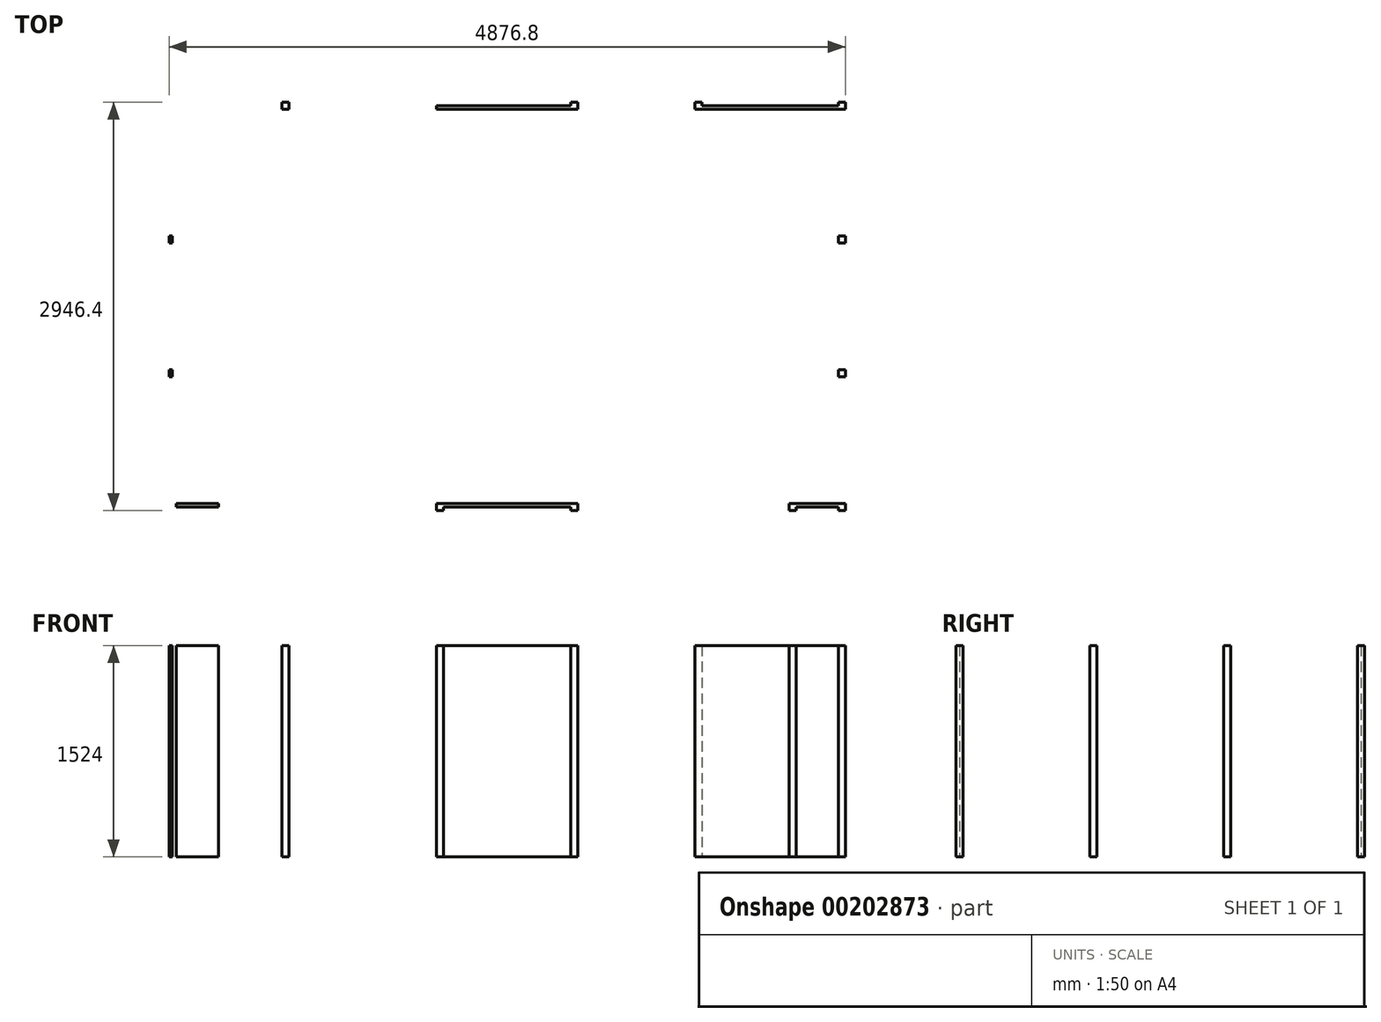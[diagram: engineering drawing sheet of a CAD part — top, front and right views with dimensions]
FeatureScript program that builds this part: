
annotation { "Feature Type Name" : "Feature", "Feature Type Description" : "" }
export const myFeature = defineFeature(function(context is Context, id is Id, definition is map)
    precondition{}
    {
        {
            var Q0;
            Q0=qCreatedBy(makeId("Top.planeOp"),FACE);
            var sketch = newSketch(context, id + "F0", { "sketchPlane" : qUnion([Q0])});
            skLineSegment(sketch, "E0.bottom", {"start": v(-61.33, -50.8) * mm, "end": v(-10.53, -50.8) * mm});
            skLineSegment(sketch, "E0.top", {"start": v(-61.33, 0) * mm, "end": v(-10.53, 0) * mm});
            skLineSegment(sketch, "E0.left", {"start": v(-61.33, -50.8) * mm, "end": v(-61.33, 0) * mm});
            skLineSegment(sketch, "E0.right", {"start": v(-10.53, -50.8) * mm, "end": v(-10.53, 0) * mm});
            skLineSegment(sketch, "E1.bottom", {"start": v(294.27, -50.8) * mm, "end": v(345.07, -50.8) * mm});
            skLineSegment(sketch, "E1.top", {"start": v(294.27, 0) * mm, "end": v(345.07, 0) * mm});
            skLineSegment(sketch, "E1.left", {"start": v(294.27, -50.8) * mm, "end": v(294.27, 0) * mm});
            skLineSegment(sketch, "E1.right", {"start": v(345.07, -50.8) * mm, "end": v(345.07, 0) * mm});
            skLineSegment(sketch, "E2.bottom", {"start": v(1869.07, -50.8) * mm, "end": v(1919.87, -50.8) * mm});
            skLineSegment(sketch, "E2.top", {"start": v(1869.07, 0) * mm, "end": v(1919.87, 0) * mm});
            skLineSegment(sketch, "E2.left", {"start": v(1869.07, -50.8) * mm, "end": v(1869.07, 0) * mm});
            skLineSegment(sketch, "E2.right", {"start": v(1919.87, -50.8) * mm, "end": v(1919.87, 0) * mm});
            skLineSegment(sketch, "E3.bottom", {"start": v(-61.33, 914.4) * mm, "end": v(-10.53, 914.4) * mm});
            skLineSegment(sketch, "E3.top", {"start": v(-61.33, 965.2) * mm, "end": v(-10.53, 965.2) * mm});
            skLineSegment(sketch, "E3.left", {"start": v(-61.33, 914.4) * mm, "end": v(-61.33, 965.2) * mm});
            skLineSegment(sketch, "E3.right", {"start": v(-10.53, 914.4) * mm, "end": v(-10.53, 965.2) * mm});
            skLineSegment(sketch, "E4.MirrorCS", {"start": v(4815.47, 965.2) * mm, "end": v(4764.67, 965.2) * mm});
            skLineSegment(sketch, "E5.MirrorCS", {"start": v(4764.67, 914.4) * mm, "end": v(4764.67, 965.2) * mm});
            skLineSegment(sketch, "E6.MirrorCS", {"start": v(4815.47, 914.4) * mm, "end": v(4764.67, 914.4) * mm});
            skLineSegment(sketch, "E7.MirrorCS", {"start": v(4815.47, 914.4) * mm, "end": v(4815.47, 965.2) * mm});
            skLineSegment(sketch, "E8.MirrorCS", {"start": v(4815.47, 0) * mm, "end": v(4764.67, 0) * mm});
            skLineSegment(sketch, "E9.MirrorCS", {"start": v(4459.87, 0) * mm, "end": v(4409.07, 0) * mm});
            skLineSegment(sketch, "E10.MirrorCS", {"start": v(4764.67, -50.8) * mm, "end": v(4764.67, 0) * mm});
            skLineSegment(sketch, "E11.MirrorCS", {"start": v(2885.07, -50.8) * mm, "end": v(2885.07, 0) * mm});
            skLineSegment(sketch, "E12.MirrorCS", {"start": v(2885.07, -50.8) * mm, "end": v(2834.27, -50.8) * mm});
            skLineSegment(sketch, "E13.MirrorCS", {"start": v(4815.47, -50.8) * mm, "end": v(4815.47, 0) * mm});
            skLineSegment(sketch, "E14.MirrorCS", {"start": v(4459.87, -50.8) * mm, "end": v(4409.07, -50.8) * mm});
            skLineSegment(sketch, "E15.MirrorCS", {"start": v(4459.87, -50.8) * mm, "end": v(4459.87, 0) * mm});
            skLineSegment(sketch, "E16.MirrorCS", {"start": v(4815.47, -50.8) * mm, "end": v(4764.67, -50.8) * mm});
            skLineSegment(sketch, "E17.MirrorCS", {"start": v(4409.07, -50.8) * mm, "end": v(4409.07, 0) * mm});
            skLineSegment(sketch, "E18.MirrorCS", {"start": v(2834.27, -50.8) * mm, "end": v(2834.27, 0) * mm});
            skLineSegment(sketch, "E19.MirrorCS", {"start": v(2885.07, 0) * mm, "end": v(2834.27, 0) * mm});
            skLineSegment(sketch, "E20.MirrorCS", {"start": v(1869.07, 2895.6) * mm, "end": v(1869.07, 2844.8) * mm});
            skLineSegment(sketch, "E21.MirrorCS", {"start": v(1919.87, 2895.6) * mm, "end": v(1919.87, 2844.8) * mm});
            skLineSegment(sketch, "E22.MirrorCS", {"start": v(-61.33, 1930.4) * mm, "end": v(-61.33, 1879.6) * mm});
            skLineSegment(sketch, "E23.MirrorCS", {"start": v(2885.07, 2844.8) * mm, "end": v(2834.27, 2844.8) * mm});
            skLineSegment(sketch, "E24.MirrorCS", {"start": v(2885.07, 2895.6) * mm, "end": v(2885.07, 2844.8) * mm});
            skLineSegment(sketch, "E25.MirrorCS", {"start": v(-61.33, 1930.4) * mm, "end": v(-10.53, 1930.4) * mm});
            skLineSegment(sketch, "E26.MirrorCS", {"start": v(1869.07, 2895.6) * mm, "end": v(1919.87, 2895.6) * mm});
            skLineSegment(sketch, "E27.MirrorCS", {"start": v(2885.07, 2895.6) * mm, "end": v(2834.27, 2895.6) * mm});
            skLineSegment(sketch, "E28.MirrorCS", {"start": v(-61.33, 2895.6) * mm, "end": v(-61.33, 2844.8) * mm});
            skLineSegment(sketch, "E29.MirrorCS", {"start": v(-10.53, 1930.4) * mm, "end": v(-10.53, 1879.6) * mm});
            skLineSegment(sketch, "E30.MirrorCS", {"start": v(1869.07, 2844.8) * mm, "end": v(1919.87, 2844.8) * mm});
            skLineSegment(sketch, "E31.MirrorCS", {"start": v(-61.33, 2895.6) * mm, "end": v(-10.53, 2895.6) * mm});
            skLineSegment(sketch, "E32.MirrorCS", {"start": v(-61.33, 1879.6) * mm, "end": v(-10.53, 1879.6) * mm});
            skLineSegment(sketch, "E33.MirrorCS", {"start": v(-10.53, 2895.6) * mm, "end": v(-10.53, 2844.8) * mm});
            skLineSegment(sketch, "E34.MirrorCS", {"start": v(2834.27, 2895.6) * mm, "end": v(2834.27, 2844.8) * mm});
            skLineSegment(sketch, "E35.MirrorCS", {"start": v(-61.33, 2844.8) * mm, "end": v(-10.53, 2844.8) * mm});
            skLineSegment(sketch, "E36.MirrorCS", {"start": v(4764.67, 1930.4) * mm, "end": v(4764.67, 1879.6) * mm});
            skLineSegment(sketch, "E37.MirrorCS", {"start": v(4815.47, 1879.6) * mm, "end": v(4764.67, 1879.6) * mm});
            skLineSegment(sketch, "E38.MirrorCS", {"start": v(4815.47, 1930.4) * mm, "end": v(4764.67, 1930.4) * mm});
            skLineSegment(sketch, "E39.MirrorCS", {"start": v(4815.47, 1930.4) * mm, "end": v(4815.47, 1879.6) * mm});
            skLineSegment(sketch, "E40.bottom", {"start": v(751.47, 2844.8) * mm, "end": v(802.27, 2844.8) * mm});
            skLineSegment(sketch, "E40.top", {"start": v(751.47, 2895.6) * mm, "end": v(802.27, 2895.6) * mm});
            skLineSegment(sketch, "E40.left", {"start": v(751.47, 2844.8) * mm, "end": v(751.47, 2895.6) * mm});
            skLineSegment(sketch, "E40.right", {"start": v(802.27, 2844.8) * mm, "end": v(802.27, 2895.6) * mm});
            skLineSegment(sketch, "E41.bottom", {"start": v(3780.8, 2844.8) * mm, "end": v(3730, 2844.8) * mm});
            skLineSegment(sketch, "E41.top", {"start": v(3780.8, 2895.6) * mm, "end": v(3730, 2895.6) * mm});
            skLineSegment(sketch, "E41.left", {"start": v(3780.8, 2844.8) * mm, "end": v(3780.8, 2895.6) * mm});
            skLineSegment(sketch, "E41.right", {"start": v(3730, 2844.8) * mm, "end": v(3730, 2895.6) * mm});
            skLineSegment(sketch, "E42.left", {"start": v(294.27, -25.4) * mm, "end": v(294.27, -25.4) * mm});
            skLineSegment(sketch, "E42.right", {"start": v(-10.53, -25.4) * mm, "end": v(-10.53, -25.4) * mm});
            skLineSegment(sketch, "E43.bottom", {"start": v(294.27, -25.4) * mm, "end": v(-10.53, -25.4) * mm});
            skLineSegment(sketch, "E43.top", {"start": v(294.27, 0) * mm, "end": v(-10.53, 0) * mm});
            skLineSegment(sketch, "E43.left", {"start": v(294.27, -25.4) * mm, "end": v(294.27, 0) * mm});
            skLineSegment(sketch, "E43.right", {"start": v(-10.53, -25.4) * mm, "end": v(-10.53, 0) * mm});
            skLineSegment(sketch, "E44.bottom", {"start": v(-10.53, 0) * mm, "end": v(-35.93, 0) * mm});
            skLineSegment(sketch, "E44.top", {"start": v(-10.53, 2844.8) * mm, "end": v(-35.93, 2844.8) * mm});
            skLineSegment(sketch, "E44.left", {"start": v(-10.53, 0) * mm, "end": v(-10.53, 2844.8) * mm});
            skLineSegment(sketch, "E44.right", {"start": v(-35.93, 0) * mm, "end": v(-35.93, 2844.8) * mm});
            skLineSegment(sketch, "E45.left", {"start": v(-10.53, 2844.8) * mm, "end": v(-10.53, 2870.2) * mm});
            skLineSegment(sketch, "E46.bottom", {"start": v(1919.87, 0) * mm, "end": v(2834.27, 0) * mm});
            skLineSegment(sketch, "E46.top", {"start": v(1919.87, -25.4) * mm, "end": v(2834.27, -25.4) * mm});
            skLineSegment(sketch, "E46.left", {"start": v(1919.87, 0) * mm, "end": v(1919.87, -25.4) * mm});
            skLineSegment(sketch, "E46.right", {"start": v(2834.27, 0) * mm, "end": v(2834.27, -25.4) * mm});
            skLineSegment(sketch, "E47.bottom", {"start": v(4459.87, 0) * mm, "end": v(4764.67, 0) * mm});
            skLineSegment(sketch, "E47.top", {"start": v(4459.87, -25.4) * mm, "end": v(4764.67, -25.4) * mm});
            skLineSegment(sketch, "E47.left", {"start": v(4459.87, 0) * mm, "end": v(4459.87, -25.4) * mm});
            skLineSegment(sketch, "E47.right", {"start": v(4764.67, 0) * mm, "end": v(4764.67, -25.4) * mm});
            skLineSegment(sketch, "E48.bottom", {"start": v(4764.67, 0) * mm, "end": v(4790.07, 0) * mm});
            skLineSegment(sketch, "E48.top", {"start": v(4764.67, 914.4) * mm, "end": v(4790.07, 914.4) * mm});
            skLineSegment(sketch, "E48.left", {"start": v(4764.67, 0) * mm, "end": v(4764.67, 914.4) * mm});
            skLineSegment(sketch, "E48.right", {"start": v(4790.07, 0) * mm, "end": v(4790.07, 914.4) * mm});
            skLineSegment(sketch, "E49.bottom", {"start": v(4764.67, 965.2) * mm, "end": v(4790.07, 965.2) * mm});
            skLineSegment(sketch, "E49.top", {"start": v(4764.67, 1879.6) * mm, "end": v(4790.07, 1879.6) * mm});
            skLineSegment(sketch, "E49.left", {"start": v(4764.67, 965.2) * mm, "end": v(4764.67, 1879.6) * mm});
            skLineSegment(sketch, "E49.right", {"start": v(4790.07, 965.2) * mm, "end": v(4790.07, 1879.6) * mm});
            skLineSegment(sketch, "E50.bottom", {"start": v(4764.67, 1930.4) * mm, "end": v(4790.07, 1930.4) * mm});
            skLineSegment(sketch, "E50.top", {"start": v(4764.67, 2844.8) * mm, "end": v(4790.07, 2844.8) * mm});
            skLineSegment(sketch, "E50.left", {"start": v(4764.67, 1930.4) * mm, "end": v(4764.67, 2844.8) * mm});
            skLineSegment(sketch, "E50.right", {"start": v(4790.07, 1930.4) * mm, "end": v(4790.07, 2844.8) * mm});
            skLineSegment(sketch, "E51.bottom", {"start": v(4764.67, 2844.8) * mm, "end": v(4815.47, 2844.8) * mm});
            skLineSegment(sketch, "E51.top", {"start": v(4764.67, 2895.6) * mm, "end": v(4815.47, 2895.6) * mm});
            skLineSegment(sketch, "E51.left", {"start": v(4764.67, 2844.8) * mm, "end": v(4764.67, 2895.6) * mm});
            skLineSegment(sketch, "E51.right", {"start": v(4815.47, 2844.8) * mm, "end": v(4815.47, 2895.6) * mm});
            skLineSegment(sketch, "E52.bottom", {"start": v(4764.67, 2870.2) * mm, "end": v(3780.8, 2870.2) * mm});
            skLineSegment(sketch, "E52.top", {"start": v(4764.67, 2844.8) * mm, "end": v(3780.8, 2844.8) * mm});
            skLineSegment(sketch, "E52.left", {"start": v(4764.67, 2870.2) * mm, "end": v(4764.67, 2844.8) * mm});
            skLineSegment(sketch, "E52.right", {"start": v(3780.8, 2870.2) * mm, "end": v(3780.8, 2844.8) * mm});
            skLineSegment(sketch, "E53.bottom", {"start": v(3730, 2844.8) * mm, "end": v(-10.53, 2844.8) * mm});
            skLineSegment(sketch, "E53.top", {"start": v(3730, 2870.2) * mm, "end": v(-10.53, 2870.2) * mm});
            skLineSegment(sketch, "E53.left", {"start": v(3730, 2844.8) * mm, "end": v(3730, 2870.2) * mm});
            skSolve(sketch);
        }
        {
            var Q0;
            Q0=makeQuery(id+"F0.imprint","IMPRINT",FACE,{"disambiguationData":[TD([[makeQuery(id+"F0.imprint","IMPRINT",EDGE,{"derivedFrom":sQuery(id+"F0.wireOp",EDGE,"E46.bottom")}),-1.0]])]});
            var Q1;
            {var subQ0=sQuery(id+"F0.wireOp",EDGE,"E53.bottom");var subQ1=sQuery(id+"F0.wireOp",EDGE,"E20.MirrorCS");var subQ2=makeQuery(id+"F0.imprint","INTERSECT",VERTEX,{"derivedFrom":[subQ1,subQ0]});Q1=makeQuery(id+"F0.imprint","IMPRINT",FACE,{"disambiguationData":[TD([[makeQuery(id+"F0.imprint","IMPRINT",EDGE,{"disambiguationData":[TD([[subQ2,1.0]])],"derivedFrom":subQ1}),-1.0]])]});}
            var Q2;
            Q2=makeQuery(id+"F0.imprint","IMPRINT",FACE,{"disambiguationData":[TD([[makeQuery(id+"F0.imprint","IMPRINT",EDGE,{"derivedFrom":sQuery(id+"F0.wireOp",EDGE,"E50.bottom")}),1.0]])]});
            var Q3;
            Q3=makeQuery(id+"F0.imprint","IMPRINT",FACE,{"disambiguationData":[TD([[makeQuery(id+"F0.imprint","IMPRINT",EDGE,{"derivedFrom":sQuery(id+"F0.wireOp",EDGE,"E49.bottom")}),1.0]])]});
            var Q4;
            Q4=makeQuery(id+"F0.imprint","IMPRINT",FACE,{"disambiguationData":[TD([[makeQuery(id+"F0.imprint","IMPRINT",EDGE,{"derivedFrom":sQuery(id+"F0.wireOp",EDGE,"E47.bottom")}),-1.0]])]});
            var Q5;
            {var subQ5=sQuery(id+"F0.wireOp",EDGE,"E53.left");Q5=makeQuery(id+"F0.imprint","IMPRINT",FACE,{"disambiguationData":[TD([[makeQuery(id+"F0.imprint","IMPRINT",EDGE,{"derivedFrom":subQ5}),1.0]])]});}
            var Q6;
            {var subQ5=sQuery(id+"F0.wireOp",EDGE,"E45.left");Q6=makeQuery(id+"F0.imprint","IMPRINT",FACE,{"disambiguationData":[TD([[makeQuery(id+"F0.imprint","IMPRINT",EDGE,{"derivedFrom":subQ5}),-1.0]])]});}
            var Q7;
            Q7=makeQuery(id+"F0.imprint","IMPRINT",FACE,{"disambiguationData":[TD([[makeQuery(id+"F0.imprint","IMPRINT",EDGE,{"derivedFrom":sQuery(id+"F0.wireOp",EDGE,"E52.bottom")}),1.0]])]});
            var Q8;
            Q8=makeQuery(id+"F0.imprint","IMPRINT",FACE,{"disambiguationData":[TD([[makeQuery(id+"F0.imprint","IMPRINT",EDGE,{"derivedFrom":sQuery(id+"F0.wireOp",EDGE,"E43.bottom")}),-1.0]])]});
            var Q9;
            {var subQ0=sQuery(id+"F0.wireOp",EDGE,"E53.bottom");var subQ1=sQuery(id+"F0.wireOp",EDGE,"E21.MirrorCS");var subQ2=makeQuery(id+"F0.imprint","INTERSECT",VERTEX,{"derivedFrom":[subQ1,subQ0]});Q9=makeQuery(id+"F0.imprint","IMPRINT",FACE,{"disambiguationData":[TD([[makeQuery(id+"F0.imprint","IMPRINT",EDGE,{"disambiguationData":[TD([[subQ2,1.0]])],"derivedFrom":subQ1}),1.0]])]});}
            var Q10;
            Q10=makeQuery(id+"F0.imprint","IMPRINT",FACE,{"disambiguationData":[TD([[makeQuery(id+"F0.imprint","IMPRINT",EDGE,{"derivedFrom":sQuery(id+"F0.wireOp",EDGE,"E48.bottom")}),1.0]])]});
            var Q11;
            {var subQ5=sQuery(id+"F0.wireOp",EDGE,"E44.top");Q11=makeQuery(id+"F0.imprint","IMPRINT",FACE,{"disambiguationData":[TD([[makeQuery(id+"F0.imprint","IMPRINT",EDGE,{"derivedFrom":subQ5}),1.0]])]});}
            var Q12;
            {var subQ5=sQuery(id+"F0.wireOp",EDGE,"E44.bottom");Q12=makeQuery(id+"F0.imprint","IMPRINT",FACE,{"disambiguationData":[TD([[makeQuery(id+"F0.imprint","IMPRINT",EDGE,{"derivedFrom":subQ5}),-1.0]])]});}
            var Q13;
            {var subQ0=sQuery(id+"F0.wireOp",EDGE,"E44.left");var subQ1=sQuery(id+"F0.wireOp",EDGE,"E3.top");var subQ2=makeQuery(id+"F0.imprint","INTERSECT",VERTEX,{"derivedFrom":[subQ1,subQ0]});Q13=makeQuery(id+"F0.imprint","IMPRINT",FACE,{"disambiguationData":[TD([[makeQuery(id+"F0.imprint","IMPRINT",EDGE,{"disambiguationData":[TD([[subQ2,1.0]])],"derivedFrom":subQ1}),1.0]])]});}
            var Q14;
            {var subQ0=sQuery(id+"F0.wireOp",EDGE,"E53.bottom");var subQ1=sQuery(id+"F0.wireOp",EDGE,"E40.left");var subQ2=makeQuery(id+"F0.imprint","INTERSECT",VERTEX,{"derivedFrom":[subQ1,subQ0]});Q14=makeQuery(id+"F0.imprint","IMPRINT",FACE,{"disambiguationData":[TD([[makeQuery(id+"F0.imprint","IMPRINT",EDGE,{"disambiguationData":[TD([[subQ2,-1.0]])],"derivedFrom":subQ1}),-1.0]])]});}
            var Q15;
            {var subQ0=sQuery(id+"F0.wireOp",EDGE,"E40.top");Q15=makeQuery(id+"F0.imprint","IMPRINT",FACE,{"disambiguationData":[TD([[makeQuery(id+"F0.imprint","IMPRINT",EDGE,{"derivedFrom":subQ0}),-1.0]])]});}
            var Q16;
            {var subQ0=sQuery(id+"F0.wireOp",EDGE,"E53.bottom");var subQ1=sQuery(id+"F0.wireOp",EDGE,"E24.MirrorCS");var subQ2=makeQuery(id+"F0.imprint","INTERSECT",VERTEX,{"derivedFrom":[subQ1,subQ0]});Q16=makeQuery(id+"F0.imprint","IMPRINT",FACE,{"disambiguationData":[TD([[makeQuery(id+"F0.imprint","IMPRINT",EDGE,{"disambiguationData":[TD([[subQ2,1.0]])],"derivedFrom":subQ1}),-1.0]])]});}
            var Q17;
            Q17=makeQuery(id+"F0.imprint","IMPRINT",FACE,{"disambiguationData":[TD([[makeQuery(id+"F0.imprint","IMPRINT",EDGE,{"derivedFrom":sQuery(id+"F0.wireOp",EDGE,"E36.MirrorCS")}),1.0]])]});
            var Q18;
            {var subQ0=sQuery(id+"F0.wireOp",EDGE,"E27.MirrorCS");Q18=makeQuery(id+"F0.imprint","IMPRINT",FACE,{"disambiguationData":[TD([[makeQuery(id+"F0.imprint","IMPRINT",EDGE,{"derivedFrom":subQ0}),1.0]])]});}
            var Q19;
            {var subQ0=sQuery(id+"F0.wireOp",EDGE,"E53.bottom");var subQ1=sQuery(id+"F0.wireOp",EDGE,"E21.MirrorCS");var subQ2=makeQuery(id+"F0.imprint","INTERSECT",VERTEX,{"derivedFrom":[subQ1,subQ0]});Q19=makeQuery(id+"F0.imprint","IMPRINT",FACE,{"disambiguationData":[TD([[makeQuery(id+"F0.imprint","IMPRINT",EDGE,{"disambiguationData":[TD([[subQ2,1.0]])],"derivedFrom":subQ1}),-1.0]])]});}
            var Q20;
            Q20=makeQuery(id+"F0.imprint","IMPRINT",FACE,{"disambiguationData":[TD([[makeQuery(id+"F0.imprint","IMPRINT",EDGE,{"derivedFrom":sQuery(id+"F0.wireOp",EDGE,"E5.MirrorCS")}),-1.0]])]});
            var Q21;
            {var subQ0=sQuery(id+"F0.wireOp",EDGE,"E44.left");var subQ1=sQuery(id+"F0.wireOp",EDGE,"E3.top");var subQ2=makeQuery(id+"F0.imprint","INTERSECT",VERTEX,{"derivedFrom":[subQ1,subQ0]});Q21=makeQuery(id+"F0.imprint","IMPRINT",FACE,{"disambiguationData":[TD([[makeQuery(id+"F0.imprint","IMPRINT",EDGE,{"disambiguationData":[TD([[subQ2,1.0]])],"derivedFrom":subQ1}),-1.0]])]});}
            var Q22;
            {var subQ0=sQuery(id+"F0.wireOp",EDGE,"E3.left");Q22=makeQuery(id+"F0.imprint","IMPRINT",FACE,{"disambiguationData":[TD([[makeQuery(id+"F0.imprint","IMPRINT",EDGE,{"derivedFrom":subQ0}),-1.0]])]});}
            var Q23;
            {var subQ0=sQuery(id+"F0.wireOp",EDGE,"E26.MirrorCS");Q23=makeQuery(id+"F0.imprint","IMPRINT",FACE,{"disambiguationData":[TD([[makeQuery(id+"F0.imprint","IMPRINT",EDGE,{"derivedFrom":subQ0}),-1.0]])]});}
            var Q24;
            Q24=makeQuery(id+"F0.imprint","IMPRINT",FACE,{"disambiguationData":[TD([[makeQuery(id+"F0.imprint","IMPRINT",EDGE,{"derivedFrom":sQuery(id+"F0.wireOp",EDGE,"E14.MirrorCS")}),-1.0]])]});
            var Q25;
            Q25=makeQuery(id+"F0.imprint","IMPRINT",FACE,{"disambiguationData":[TD([[makeQuery(id+"F0.imprint","IMPRINT",EDGE,{"derivedFrom":sQuery(id+"F0.wireOp",EDGE,"E41.bottom")}),-1.0]])]});
            var Q26;
            {var subQ0=sQuery(id+"F0.wireOp",EDGE,"E22.MirrorCS");Q26=makeQuery(id+"F0.imprint","IMPRINT",FACE,{"disambiguationData":[TD([[makeQuery(id+"F0.imprint","IMPRINT",EDGE,{"derivedFrom":subQ0}),1.0]])]});}
            var Q27;
            {var subQ0=sQuery(id+"F0.wireOp",EDGE,"E44.left");var subQ1=sQuery(id+"F0.wireOp",EDGE,"E25.MirrorCS");var subQ2=makeQuery(id+"F0.imprint","INTERSECT",VERTEX,{"derivedFrom":[subQ1,subQ0]});Q27=makeQuery(id+"F0.imprint","IMPRINT",FACE,{"disambiguationData":[TD([[makeQuery(id+"F0.imprint","IMPRINT",EDGE,{"disambiguationData":[TD([[subQ2,1.0]])],"derivedFrom":subQ1}),-1.0]])]});}
            var Q28;
            Q28=makeQuery(id+"F0.imprint","IMPRINT",FACE,{"disambiguationData":[TD([[makeQuery(id+"F0.imprint","IMPRINT",EDGE,{"derivedFrom":sQuery(id+"F0.wireOp",EDGE,"E51.top")}),-1.0]])]});
            var Q29;
            Q29=makeQuery(id+"F0.imprint","IMPRINT",FACE,{"disambiguationData":[TD([[makeQuery(id+"F0.imprint","IMPRINT",EDGE,{"derivedFrom":sQuery(id+"F0.wireOp",EDGE,"E19.MirrorCS")}),1.0]])]});
            var Q30;
            Q30=makeQuery(id+"F0.imprint","IMPRINT",FACE,{"disambiguationData":[TD([[makeQuery(id+"F0.imprint","IMPRINT",EDGE,{"derivedFrom":sQuery(id+"F0.wireOp",EDGE,"E13.MirrorCS")}),1.0]])]});
            var Q31;
            Q31=makeQuery(id+"F0.imprint","IMPRINT",FACE,{"disambiguationData":[TD([[makeQuery(id+"F0.imprint","IMPRINT",EDGE,{"derivedFrom":sQuery(id+"F0.wireOp",EDGE,"E2.right")}),1.0]])]});
            var Q32;
            Q32=makeQuery(id+"F0.imprint","IMPRINT",FACE,{"disambiguationData":[TD([[makeQuery(id+"F0.imprint","IMPRINT",EDGE,{"derivedFrom":sQuery(id+"F0.wireOp",EDGE,"E1.right")}),1.0]])]});
            var Q33;
            Q33=makeQuery(id+"F0.imprint","IMPRINT",FACE,{"disambiguationData":[TD([[makeQuery(id+"F0.imprint","IMPRINT",EDGE,{"derivedFrom":sQuery(id+"F0.wireOp",EDGE,"E0.left")}),-1.0]])]});
            var Q34;
            Q34=makeQuery(id+"F0.imprint","IMPRINT",FACE,{"disambiguationData":[TD([[makeQuery(id+"F0.imprint","IMPRINT",EDGE,{"derivedFrom":sQuery(id+"F0.wireOp",EDGE,"E31.MirrorCS")}),-1.0]])]});
            extrude(context, id + "F1", {"entities" : qUnion([Q0, Q1, Q2, Q3, Q4, Q5, Q6, Q7, Q8, Q9, Q10, Q11, Q12, Q13, Q14, Q15, Q16, Q17, Q18, Q19, Q20, Q21, Q22, Q23, Q24, Q25, Q26, Q27, Q28, Q29, Q30, Q31, Q32, Q33, Q34]), "depth" : 1524 * mm});
        }
    });
